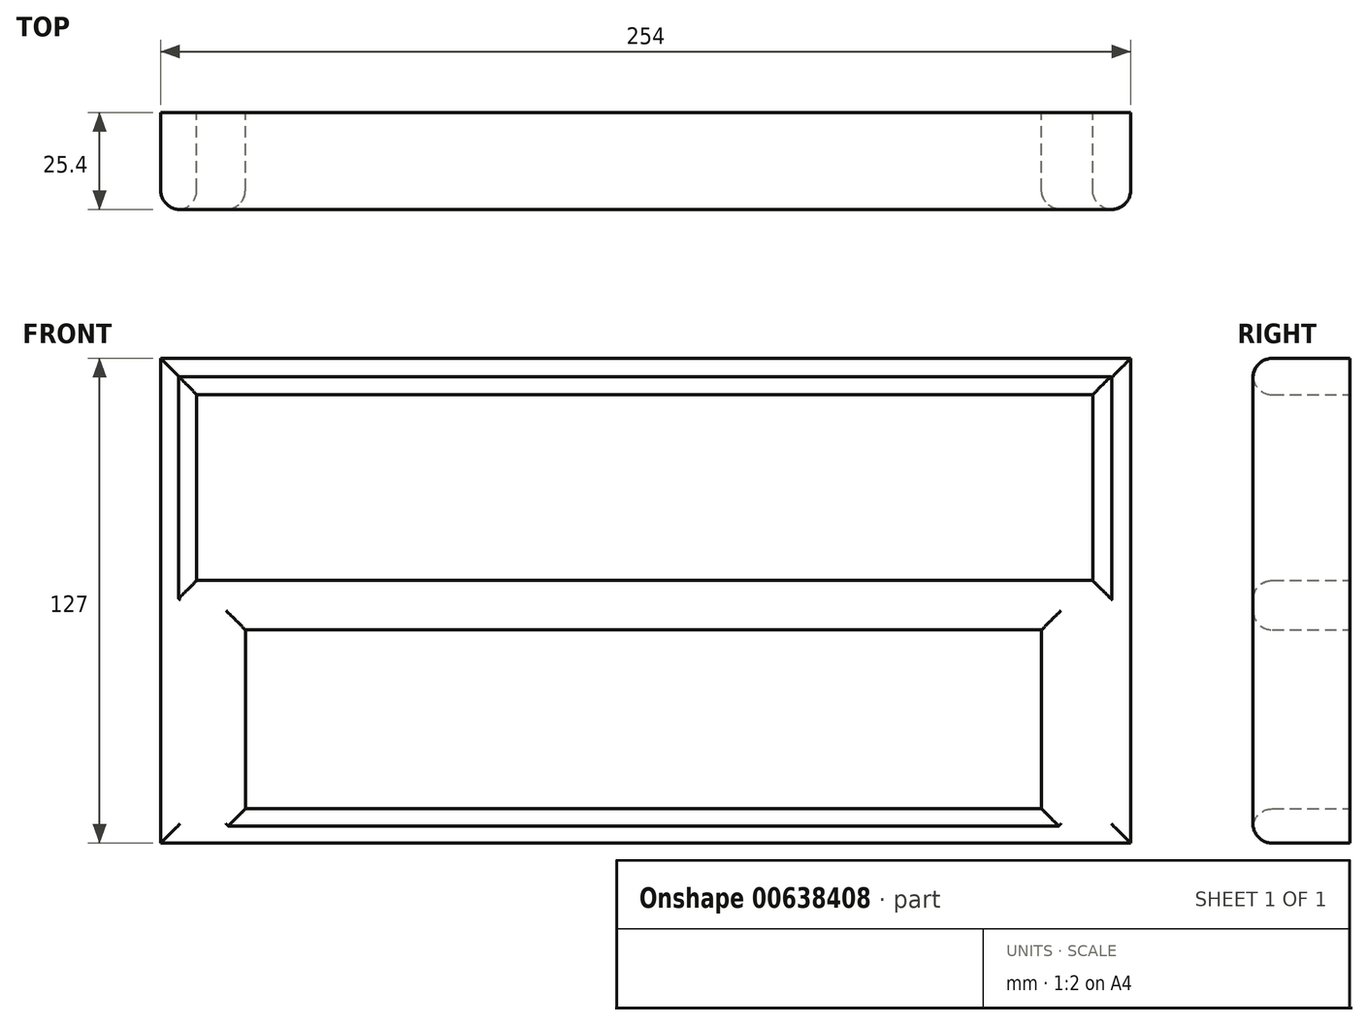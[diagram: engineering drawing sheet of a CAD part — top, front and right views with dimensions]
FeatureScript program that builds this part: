
annotation { "Feature Type Name" : "Feature", "Feature Type Description" : "" }
export const myFeature = defineFeature(function(context is Context, id is Id, definition is map)
    precondition{}
    {
        {
            var Q0;
            Q0=qCreatedBy(makeId("Front.planeOp"),FACE);
            var sketch = newSketch(context, id + "F0", { "sketchPlane" : qUnion([Q0])});
            skLineSegment(sketch, "E0.bottom", {"start": v(127, -63.5) * mm, "end": v(-127, -63.5) * mm});
            skLineSegment(sketch, "E0.top", {"start": v(127, 63.5) * mm, "end": v(-127, 63.5) * mm});
            skLineSegment(sketch, "E0.left", {"start": v(127, -63.5) * mm, "end": v(127, 63.5) * mm});
            skLineSegment(sketch, "E0.right", {"start": v(-127, -63.5) * mm, "end": v(-127, 63.5) * mm});
            skPoint(sketch, "E0.middle", {"position": v(0, 0) * mm});
            skSolve(sketch);
        }
        {
            var Q0;
            Q0=makeQuery(id+"F0.imprint","IMPRINT",FACE,{"disambiguationData":[TD([[makeQuery(id+"F0.imprint","IMPRINT",EDGE,{"derivedFrom":sQuery(id+"F0.wireOp",EDGE,"E0.bottom")}),-1.0]])]});
            var sketch = newSketch(context, id + "F1", { "sketchPlane" : qUnion([Q0])});
            skLineSegment(sketch, "E1.bottom", {"start": v(-117.55, 53.99) * mm, "end": v(117.04, 53.99) * mm});
            skLineSegment(sketch, "E1.top", {"start": v(-117.55, 5.32) * mm, "end": v(117.04, 5.32) * mm});
            skLineSegment(sketch, "E1.left", {"start": v(-117.55, 53.99) * mm, "end": v(-117.55, 5.32) * mm});
            skLineSegment(sketch, "E1.right", {"start": v(117.04, 53.99) * mm, "end": v(117.04, 5.32) * mm});
            skLineSegment(sketch, "E2.bottom", {"start": v(-104.83, -7.62) * mm, "end": v(103.66, -7.62) * mm});
            skLineSegment(sketch, "E2.top", {"start": v(-104.83, -54.54) * mm, "end": v(103.66, -54.54) * mm});
            skLineSegment(sketch, "E2.left", {"start": v(-104.83, -7.62) * mm, "end": v(-104.83, -54.54) * mm});
            skLineSegment(sketch, "E2.right", {"start": v(103.66, -7.62) * mm, "end": v(103.66, -54.54) * mm});
            skSolve(sketch);
        }
        {
            var Q0;
            Q0=makeQuery(id+"F0.imprint","IMPRINT",FACE,{"disambiguationData":[TD([[makeQuery(id+"F0.imprint","IMPRINT",EDGE,{"derivedFrom":sQuery(id+"F0.wireOp",EDGE,"E0.bottom")}),-1.0]])]});
            extrude(context, id + "F2", {"entities" : qUnion([Q0]), "depth" : 25.4 * mm, "offsetDistance" : 25.4 * mm});
        }
        {
            var Q0;
            Q0 = qSketchRegion(id + "F1", true);
            extrude(context, id + "F3", {"entities" : qUnion([Q0]), "operationType" : NewBodyOperationType.REMOVE, "oppositeDirection" : true, "depth" : 50.8 * mm, "offsetDistance" : 25.4 * mm});
        }
        {
            var Q0;
            Q0 = qSketchRegion(id + "F1", true);
            extrude(context, id + "F4", {"entities" : qUnion([Q0]), "operationType" : NewBodyOperationType.REMOVE, "depth" : 102.87 * mm, "offsetDistance" : 25.4 * mm});
        }
        {
            var Q0;
            Q0=makeQuery(id+"F2.opExtrude","CAP_FACE",FACE,{"disambiguationData":[OSD([sQuery(id+"F0.wireOp",EDGE,"E0.bottom"),sQuery(id+"F0.wireOp",EDGE,"E0.top"),sQuery(id+"F0.wireOp",EDGE,"E0.left"),sQuery(id+"F0.wireOp",EDGE,"E0.right")])],"isStart":false});
            fillet(context, id + "F5", {"entities" : qUnion([Q0]), "radius" : 5.08 * mm, "tangentPropagation" : true, "allowEdgeOverflow" : false});
        }
    });
